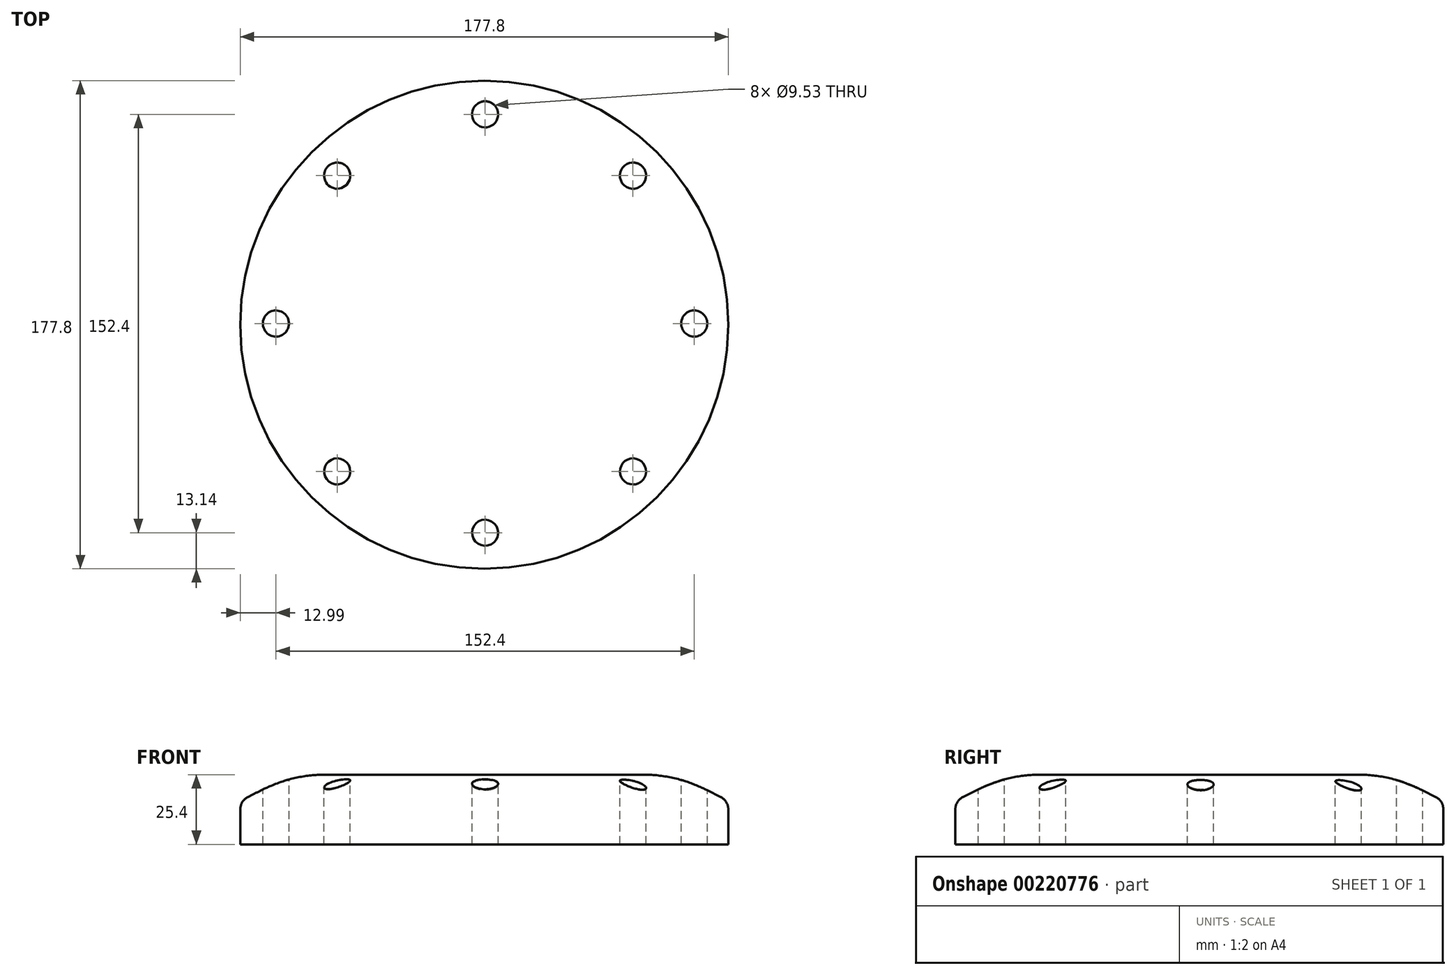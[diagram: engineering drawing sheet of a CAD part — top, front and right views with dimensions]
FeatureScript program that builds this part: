
annotation { "Feature Type Name" : "Feature", "Feature Type Description" : "" }
export const myFeature = defineFeature(function(context is Context, id is Id, definition is map)
    precondition{}
    {
        {
            var Q0;
            Q0=qCreatedBy(makeId("Top.planeOp"),FACE);
            var sketch = newSketch(context, id + "F0", { "sketchPlane" : qUnion([Q0])});
            skCircle(sketch, "E0", {"center": v(-0.3, -0.44) * mm, "radius": 88.9 * mm});
            skSolve(sketch);
        }
        {
            var Q0;
            Q0=makeQuery(id+"F0.imprint","IMPRINT",FACE,{"disambiguationData":[TD([[makeQuery(id+"F0.imprint","IMPRINT",EDGE,{"derivedFrom":sQuery(id+"F0.wireOp",EDGE,"E0")}),1.0]])]});
            extrude(context, id + "F1", {"entities" : qUnion([Q0]), "depth" : 25.4 * mm});
        }
        {
            var Q0;
            Q0=makeQuery(id+"F1.opExtrude","CAP_FACE",FACE,{"disambiguationData":[OSD([sQuery(id+"F0.wireOp",EDGE,"E0")])],"isStart":false});
            var sketch = newSketch(context, id + "F2", { "sketchPlane" : qUnion([Q0])});
            skCircle(sketch, "E1", {"center": v(0, 0) * mm, "radius": 76.2 * mm, "construction": true});
            skCircle(sketch, "E2", {"center": v(76.2, 0) * mm, "radius": 4.76 * mm});
            skCircle(sketch, "E3.1.0", {"center": v(53.88, 53.88) * mm, "radius": 4.76 * mm});
            skCircle(sketch, "E3.2.0", {"center": v(0, 76.2) * mm, "radius": 4.76 * mm});
            skCircle(sketch, "E3.3.0", {"center": v(-53.88, 53.88) * mm, "radius": 4.76 * mm});
            skCircle(sketch, "E3.4.0", {"center": v(-76.2, 0) * mm, "radius": 4.76 * mm});
            skCircle(sketch, "E3.5.0", {"center": v(-53.88, -53.88) * mm, "radius": 4.76 * mm});
            skCircle(sketch, "E3.6.0", {"center": v(0, -76.2) * mm, "radius": 4.76 * mm});
            skCircle(sketch, "E3.7.0", {"center": v(53.88, -53.88) * mm, "radius": 4.76 * mm});
            skSolve(sketch);
        }
        {
            var Q0;
            Q0 = qSketchRegion(id + "F2", true);
            extrude(context, id + "F3", {"entities" : qUnion([Q0]), "operationType" : NewBodyOperationType.REMOVE, "endBound" : BoundingType.THROUGH_ALL, "oppositeDirection" : true, "depth" : 25.4 * mm});
        }
        {
            var Q0;
            Q0=makeQuery(id+"F1.opExtrude","CAP_EDGE",EDGE,{"disambiguationData":[OSD([sQuery(id+"F0.wireOp",EDGE,"E0")])],"isStart":false});
            chamfer(context, id + "F4", {"entities" : qUnion([Q0]), "chamferType" : ChamferType.TWO_OFFSETS, "width1" : 19.05 * mm, "oppositeDirection" : false, "width2" : 9.52 * mm, "tangentPropagation" : true});
        }
        {
            var Q0;
            {var subQ0=sQuery(id+"F0.wireOp",EDGE,"E0");Q0=makeQuery(id+"F4.opChamfer","BLEND_EDGE",EDGE,{"blendedFrom":[makeQuery(id+"F1.opExtrude","CAP_EDGE",EDGE,{"disambiguationData":[OSD([subQ0])],"isStart":false}),makeQuery(id+"F1.opExtrude","CAP_FACE",FACE,{"disambiguationData":[OSD([subQ0])],"isStart":false})],"blendedInto":[makeQuery(id+"F1.opExtrude","CAP_FACE",FACE,{"disambiguationData":[OSD([subQ0])],"isStart":false})]});}
            fillet(context, id + "F5", {"entities" : qUnion([Q0]), "radius" : 50.8 * mm, "tangentPropagation" : true, "allowEdgeOverflow" : false});
        }
        {
            var Q0;
            {var subQ0=sQuery(id+"F0.wireOp",EDGE,"E0");Q0=makeQuery(id+"F4.opChamfer","BLEND_EDGE",EDGE,{"blendedFrom":[makeQuery(id+"F1.opExtrude","CAP_EDGE",EDGE,{"disambiguationData":[OSD([subQ0])],"isStart":false}),makeQuery(id+"F1.opExtrude","SWEPT_FACE",FACE,{"disambiguationData":[OSD([subQ0])]})],"blendedInto":[makeQuery(id+"F1.opExtrude","SWEPT_FACE",FACE,{"disambiguationData":[OSD([subQ0])]})]});}
            fillet(context, id + "F6", {"entities" : qUnion([Q0]), "radius" : 5.08 * mm, "tangentPropagation" : true, "allowEdgeOverflow" : false});
        }
    });
